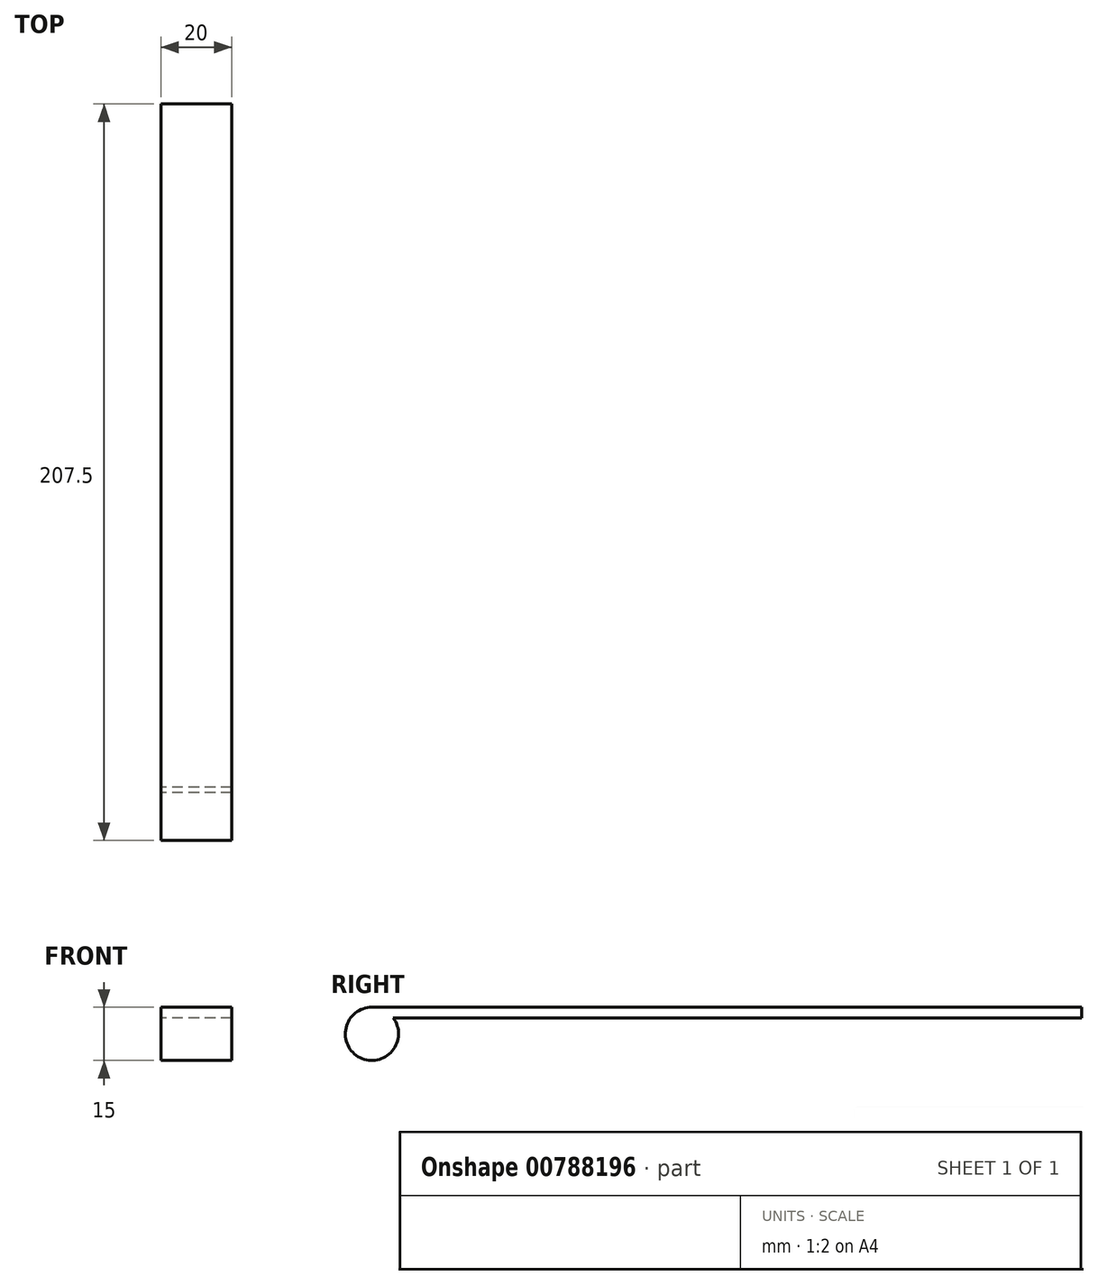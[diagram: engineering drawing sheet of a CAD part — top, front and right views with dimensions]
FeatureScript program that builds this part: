
annotation { "Feature Type Name" : "Feature", "Feature Type Description" : "" }
export const myFeature = defineFeature(function(context is Context, id is Id, definition is map)
    precondition{}
    {
        {
            var Q0;
            Q0=qCreatedBy(makeId("Right.planeOp"),FACE);
            var sketch = newSketch(context, id + "F0", { "sketchPlane" : qUnion([Q0])});
            skCircle(sketch, "E0", {"center": v(0, 0) * mm, "radius": 7.5 * mm});
            skLineSegment(sketch, "E1.bottom", {"start": v(0, 7.5) * mm, "end": v(200, 7.5) * mm});
            skLineSegment(sketch, "E1.top", {"start": v(0, 4.5) * mm, "end": v(200, 4.5) * mm});
            skLineSegment(sketch, "E1.left", {"start": v(0, 7.5) * mm, "end": v(0, 4.5) * mm});
            skLineSegment(sketch, "E1.right", {"start": v(200, 7.5) * mm, "end": v(200, 4.5) * mm});
            skSolve(sketch);
        }
        {
            var Q0;
            {var subQ0=sQuery(id+"F0.wireOp",EDGE,"E1.bottom");Q0=makeQuery(id+"F0.imprint","IMPRINT",FACE,{"disambiguationData":[TD([[makeQuery(id+"F0.imprint","IMPRINT",EDGE,{"derivedFrom":subQ0}),-1.0]])]});}
            var Q1;
            {var subQ0=sQuery(id+"F0.wireOp",EDGE,"E1.left");Q1=makeQuery(id+"F0.imprint","IMPRINT",FACE,{"disambiguationData":[TD([[makeQuery(id+"F0.imprint","IMPRINT",EDGE,{"derivedFrom":subQ0}),1.0]])]});}
            var Q2;
            {var subQ0=sQuery(id+"F0.wireOp",EDGE,"E1.left");Q2=makeQuery(id+"F0.imprint","IMPRINT",FACE,{"disambiguationData":[TD([[makeQuery(id+"F0.imprint","IMPRINT",EDGE,{"derivedFrom":subQ0}),-1.0]])]});}
            extrude(context, id + "F1", {"entities" : qUnion([Q0, Q1, Q2]), "depth" : 20 * mm, "offsetDistance" : 25 * mm});
        }
        {
            var Q0;
            Q0=makeQuery(id+"F1.opExtrude","SWEPT_FACE",FACE,{"disambiguationData":[OSD([sQuery(id+"F0.wireOp",EDGE,"E1.top")])]});
            var sketch = newSketch(context, id + "F2", { "sketchPlane" : qUnion([Q0])});
            skLineSegment(sketch, "E2", {"start": v(10, -6) * mm, "end": v(10, -200) * mm, "construction": true});
            skLineSegment(sketch, "E3", {"start": v(20, -6) * mm, "end": v(0, -200) * mm, "construction": true});
            skPoint(sketch, "E4", {"position": v(10, -103) * mm});
            skLineSegment(sketch, "E5", {"start": v(10, -6) * mm, "end": v(10, -56) * mm});
            skSolve(sketch);
        }
    });
